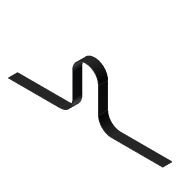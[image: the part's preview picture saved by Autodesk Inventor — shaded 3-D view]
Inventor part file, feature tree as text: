
AUTODESK INVENTOR PART (.ipt)
format: ipt  version: unknown  size: 209,920 bytes
history: native  units: in
note: dims shown in document units (in); Inventor stores cm internally (conversion verified against a paired STEP export)
features: sketch x5, extrude x2, plane x1, sweep x1
ambient origin geometry x8: Origin, YZ Plane, XZ Plane, XY Plane, X Axis, Y Axis, Z Axis, Center Point
feature tree (9):
  sketch  "Sketch9"  dims[d49=3.937in d50=15.748in]
  sketch  "Sketch14"  dims[d51=0.7087in d52=0.3543in]
  plane  "Work Plane8"
  sweep  "Sweep7"
  extrude  "Extrusion5"  Depth=0.3543in
  extrude  "Extrusion6"  Depth=0.0394in
  sketch  "Sketch16"  dims[d53=0.0197in d54=0.0394in]
  sketch  "Sketch17"  dims[d58=0.9843in]
  sketch  "Sketch18"  dims[d59=1.9685in d60=1.9685in d61=1.9685in d62=1.9685in d64=7.874in d65=7.874in d66=0.7087in d67=0.3543in d68=0.0197in d69=0.0394in d70=0.0in d71=3.937in d72=0.0in d73=3.937in d74=0.0in]
